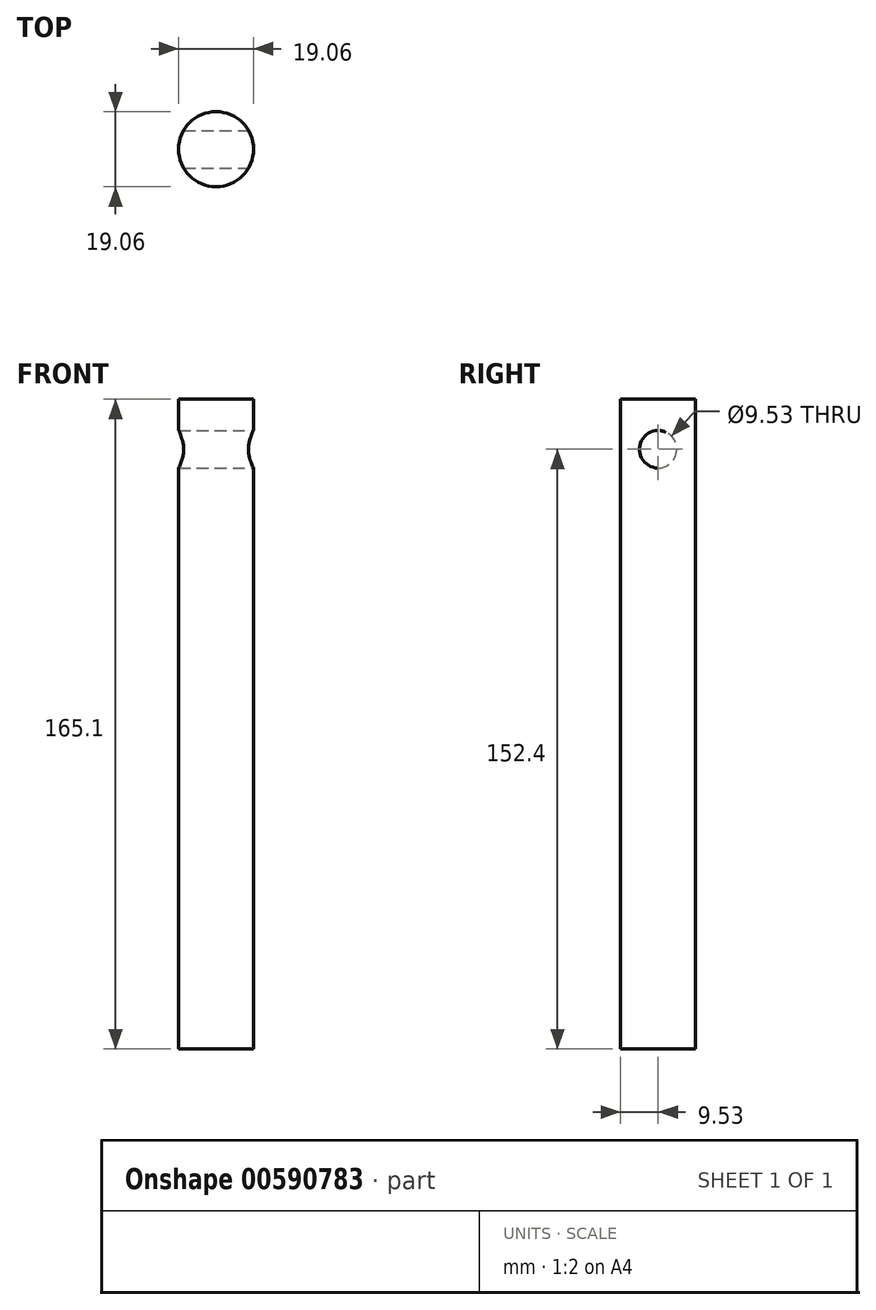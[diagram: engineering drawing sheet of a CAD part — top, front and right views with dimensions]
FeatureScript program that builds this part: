
annotation { "Feature Type Name" : "Feature", "Feature Type Description" : "" }
export const myFeature = defineFeature(function(context is Context, id is Id, definition is map)
    precondition{}
    {
        {
            var Q0;
            Q0=qCreatedBy(makeId("Top.planeOp"),FACE);
            var sketch = newSketch(context, id + "F0", { "sketchPlane" : qUnion([Q0])});
            skCircle(sketch, "E0", {"center": v(0, 0) * mm, "radius": 9.53 * mm});
            skSolve(sketch);
        }
        {
            var Q0;
            Q0 = qSketchRegion(id + "F0", true);
            extrude(context, id + "F1", {"entities" : qUnion([Q0]), "depth" : 165.1 * mm, "offsetDistance" : 25.4 * mm});
        }
        {
            var Q0;
            Q0=qCreatedBy(makeId("Right.planeOp"),FACE);
            var sketch = newSketch(context, id + "F2", { "sketchPlane" : qUnion([Q0])});
            skCircle(sketch, "E1", {"center": v(0, 152.4) * mm, "radius": 4.76 * mm});
            skSolve(sketch);
        }
        {
            var Q0;
            Q0 = qSketchRegion(id + "F2", true);
            extrude(context, id + "F3", {"entities" : qUnion([Q0]), "operationType" : NewBodyOperationType.REMOVE, "endBound" : BoundingType.THROUGH_ALL, "oppositeDirection" : true, "depth" : 25.4 * mm, "offsetDistance" : 25.4 * mm, "hasSecondDirection" : true, "secondDirectionBound" : SecondDirectionBoundingType.THROUGH_ALL, "secondDirectionOppositeDirection" : false, "secondDirectionDepth" : 25.4 * mm});
        }
    });
